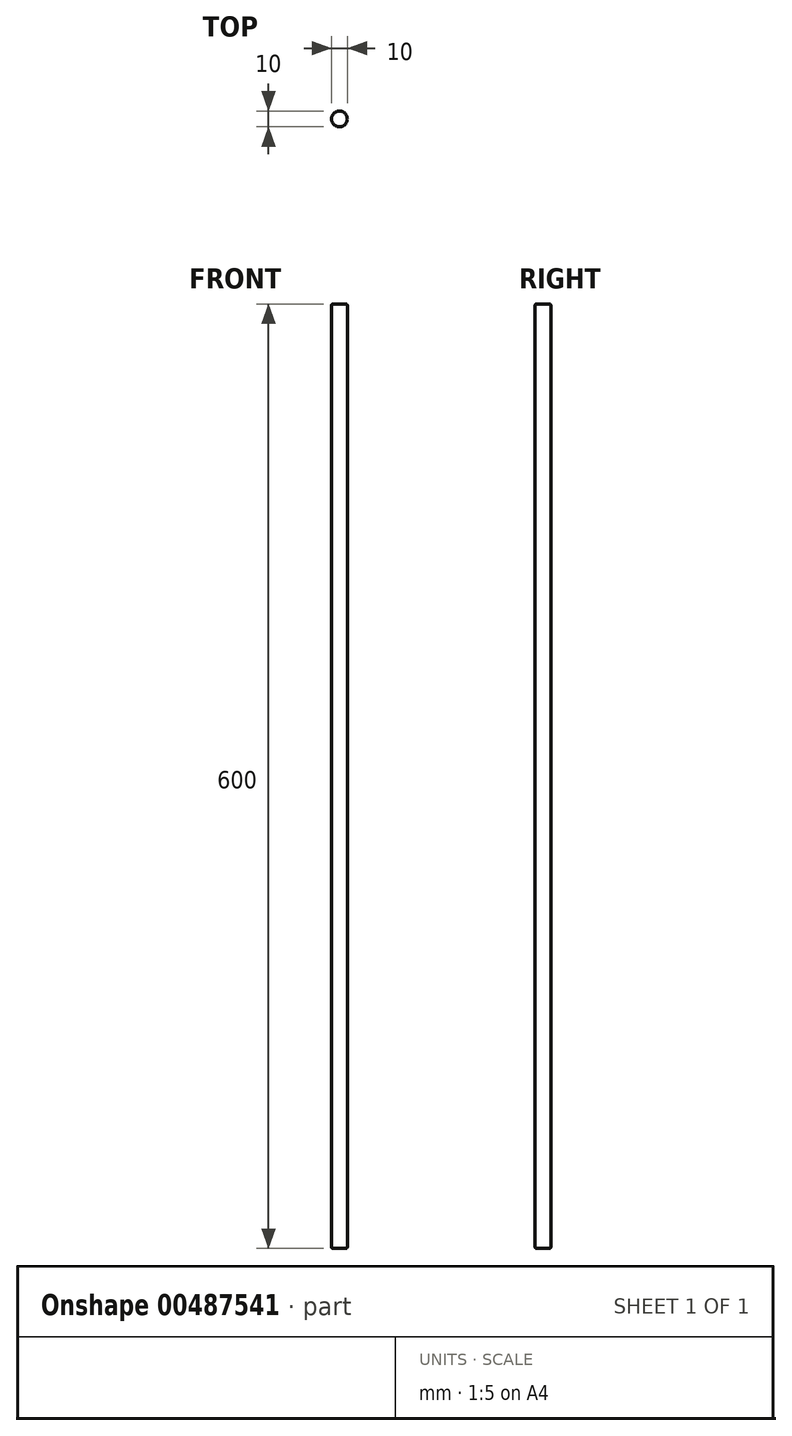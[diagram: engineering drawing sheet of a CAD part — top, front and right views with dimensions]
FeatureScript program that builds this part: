
annotation { "Feature Type Name" : "Feature", "Feature Type Description" : "" }
export const myFeature = defineFeature(function(context is Context, id is Id, definition is map)
    precondition{}
    {
        {
            var Q0;
            Q0=qCreatedBy(makeId("Top.planeOp"),FACE);
            var sketch = newSketch(context, id + "F0", { "sketchPlane" : qUnion([Q0])});
            skCircle(sketch, "E0", {"center": v(0, 0) * mm, "radius": 5 * mm});
            skSolve(sketch);
        }
        {
            var Q0;
            Q0=qSketchRegion(id+"F0",true);
            extrude(context, id + "F1", {"entities" : qUnion([Q0]), "depth" : 600 * mm, "offsetDistance" : 25 * mm});
        }
        {
            var Q0;
            Q0=makeQuery(id+"F1.opExtrude","CAP_EDGE",EDGE,{"disambiguationData":[OSD([sQuery(id+"F0.wireOp",EDGE,"E0")])],"isStart":false});
            var Q1;
            Q1=makeQuery(id+"F1.opExtrude","CAP_EDGE",EDGE,{"disambiguationData":[OSD([sQuery(id+"F0.wireOp",EDGE,"E0")])],"isStart":true});
            fillet(context, id + "F2", {"entities" : qUnion([Q0, Q1]), "radius" : 1 * mm, "tangentPropagation" : true, "allowEdgeOverflow" : false});
        }
    });
